# Revit family: PRD_FrankeWS_Snks_SIRIUSUtilitySink_BS300N_BS301N
name_source: partatom
category: Plumbing Fixtures
revit_build: Autodesk Revit 2018 (Build: 20190510_1515(x64)
units: mm (PartAtom-declared; Revit-internal decimal feet)

## family parameters
Cut with Voids When Loaded = Yes
Host = Face
OmniClass Number = 23.45.05.14.14.27
OmniClass Title = Service Sinks
Part Type = Normal
Room Calculation Point = No
Round Connector Dimension = Use Diameter
Shared = Yes

## types (2) — shared parameters
AssetType = Fixed
BowlConstruction = Radius corners
BowlDepth = 330
BowlFinish = Satin finish
BowlHeight = 200
BowlPosition = Center
BowlWidth = 395
Category = Pr_40_20_96_81, Sinks
Default Elevation = 925 mm  [stored 3.03478 ft]
DiameterNominal = 40  [stored 0.131234 ft]
DrainSize = 40 mm  [stored 0.131234 ft]
DurationUnit = year
Features = stainless steel, surface satin finished, right hand drain
Finish = Satin finished
FrameMaterial = PRD_AR_Plastic_GreyBlue
IfcExportAs = IfcSanitaryTerminalType
IfcExportType = SINK
IntegralAccessories = fixings included
Manufacturer = KWC Group AG
ManufacturerName = KWC Group AG
ManufacturerURL = www.kwc.com
Material = Stainless steel
MaterialCode = 1.4301 Chrome Nickel steel V2A
MaterialThickness = 1.00 mm
Mounting = WallHung
NBSDescription = Sinks
NBSReference = 45-35-70/344
NominalDepth = 405 mm
NominalHeight = 250 mm  [stored 0.82021 ft]
NominalWidth = 470 mm  [stored 1.54199 ft]
NumberOfWasteHoles = 1
OutletSize = G 1 1/2 B
Overflow = Standpipe overflow
ProductInformation = https://pim.kwc.com
RearUpstand = No
SinkMaterial = PRD_AR_StainlessSteel_SatinFinished
SinkType = London
Size = 470 x 250 x 405 mm (W x H x D)
Spillway = No
Splashback = No
SplashbackHeight = 44.00 mm
Sump = No
TailorMade = No
TapLedge = No
TypeOfMounting = Wall mounting
TypeOfUtilitySink = Cleaner sink
TypeOfWasteKit = Standpipe strainer
URL = www.kwc.com
Uniclass2015Code = Pr_40_20_96_81
Uniclass2015Title = Sinks
Uniclass2015Version = Products v1.17
Version = 1
WarrantyDurationUnit = year
WashRiffle = No
WasteHolePosition = Right center
WasteHoleProjection = 206.00 mm
WasteKitIncluded = Yes
WasteSize = DN 40
zero-valued in all types: MountingOffset

## per-type parameters (varying)
| type | BIMObjectName | Description | Grid | GridMaterial | GridVisibility | GrossWeight | MaterialCodeGrid | ModelNumber | Name | NetWeight | ProductCode |
| BS300N | PRD_AR_Sinks_SIRIUSUtilitySink_BS300N | SIRIUS Utility sink for wall mounting, stainless steel, surface satin finished, material thickness 1 mm, rounded edges, with grey plastic frame, with folding grid, G 1 1/2 B plastic standpipe strainer, right hand drain, with 44 mm rear upstand, fixings included. | Hinged | Stainless steel | Yes | 5.30 kg | 1.4301 Chrome Nickel steel V2A | 207.0599.542 | SIRIUS Utility sink BS300N | 4.80 kg | 207.0599.542 |
| BS301N | PRD_AR_Sinks_SIRIUSUtilitySink_BS301N | SIRIUS Utility sink for wall mounting, stainless steel, surface satin finished, material thickness 1 mm, rounded edges, with grey plastic frame, without folding grid, G 1 1/2 B plastic standpipe strainer, right hand drain, with 44 mm rear upstand, fixings included. | No |  | No | 4.60 kg |  | 207.0599.545 | SIRIUS Utility sink BS301N | 4.10 kg | 207.0599.545 |

note: column(s) folded — value = type name in every type: Model, ModelReference

note: [stored X ft] marks values corroborated as IEEE doubles in the binary element streams (Revit-internal decimal feet)

## geometry (parser evidence)
native form markers: Sweep x4
no freeform markers — native parametric forms only
